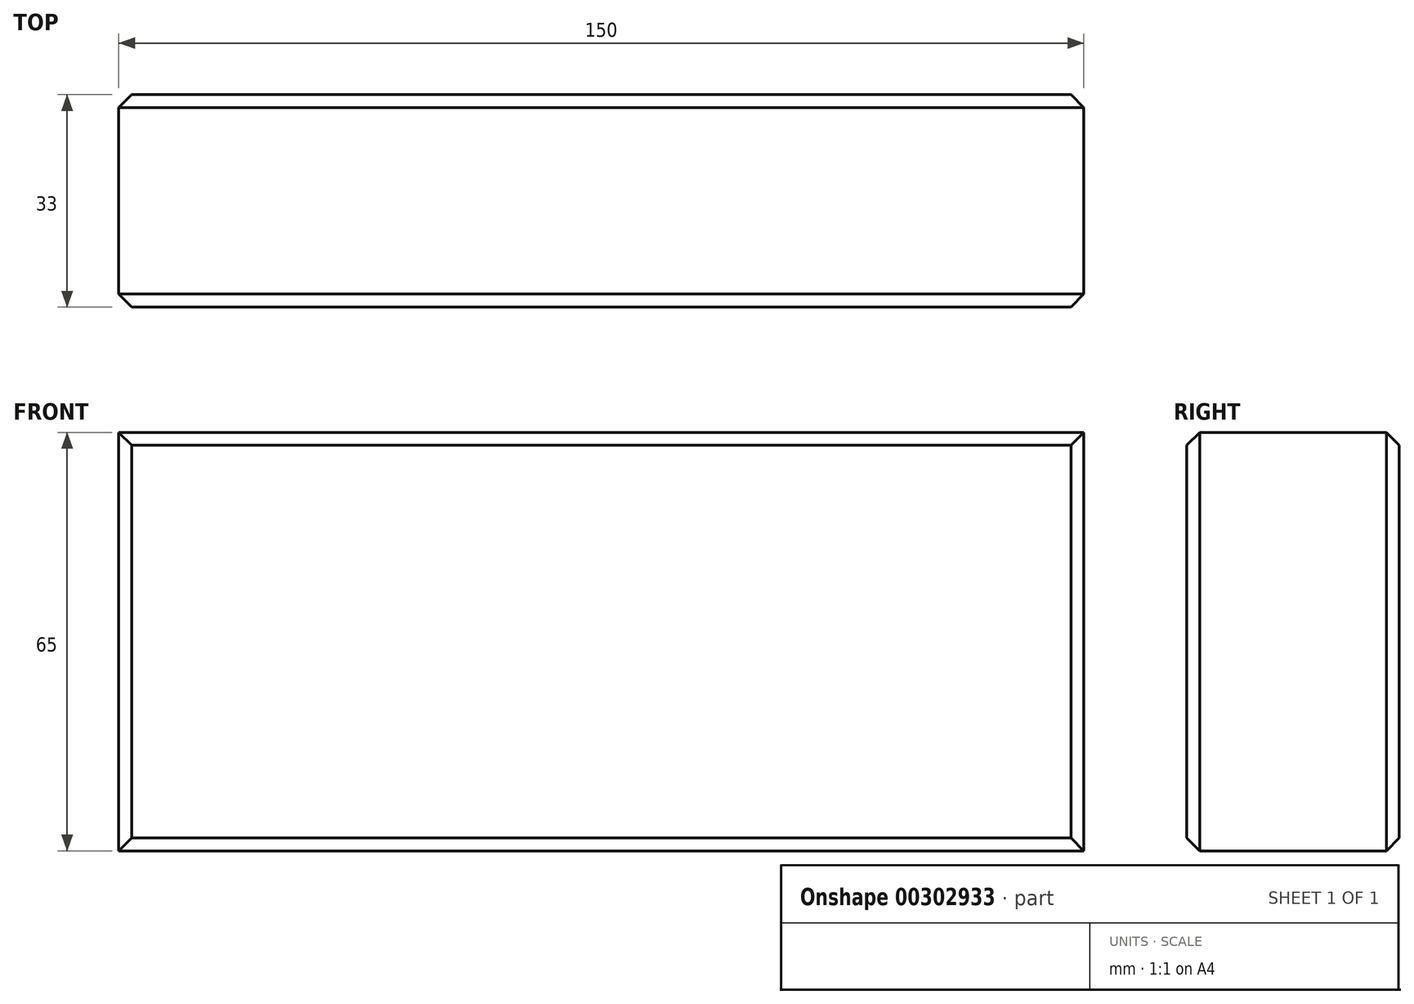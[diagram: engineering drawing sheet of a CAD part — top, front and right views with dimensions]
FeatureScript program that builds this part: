
annotation { "Feature Type Name" : "Feature", "Feature Type Description" : "" }
export const myFeature = defineFeature(function(context is Context, id is Id, definition is map)
    precondition{}
    {
        {
            var Q0;
            Q0=qCreatedBy(makeId("Front.planeOp"),FACE);
            var sketch = newSketch(context, id + "F0", { "sketchPlane" : qUnion([Q0])});
            skLineSegment(sketch, "E0.bottom", {"start": v(75, -32.5) * mm, "end": v(-75, -32.5) * mm});
            skLineSegment(sketch, "E0.top", {"start": v(75, 32.5) * mm, "end": v(-75, 32.5) * mm});
            skLineSegment(sketch, "E0.left", {"start": v(75, -32.5) * mm, "end": v(75, 32.5) * mm});
            skLineSegment(sketch, "E0.right", {"start": v(-75, -32.5) * mm, "end": v(-75, 32.5) * mm});
            skPoint(sketch, "E0.middle", {"position": v(0, 0) * mm});
            skSolve(sketch);
        }
        {
            var Q0;
            Q0 = qSketchRegion(id + "F0", true);
            extrude(context, id + "F1", {"entities" : qUnion([Q0]), "endBound" : BoundingType.SYMMETRIC, "depth" : 33 * mm});
        }
        {
            var Q0;
            Q0=makeQuery(id+"F1.opExtrude","CAP_FACE",FACE,{"disambiguationData":[OSD([sQuery(id+"F0.wireOp",EDGE,"E0.bottom"),sQuery(id+"F0.wireOp",EDGE,"E0.top"),sQuery(id+"F0.wireOp",EDGE,"E0.left"),sQuery(id+"F0.wireOp",EDGE,"E0.right")])],"isStart":false});
            var Q1;
            Q1=makeQuery(id+"F1.opExtrude","CAP_FACE",FACE,{"disambiguationData":[OSD([sQuery(id+"F0.wireOp",EDGE,"E0.bottom"),sQuery(id+"F0.wireOp",EDGE,"E0.top"),sQuery(id+"F0.wireOp",EDGE,"E0.left"),sQuery(id+"F0.wireOp",EDGE,"E0.right")])],"isStart":true});
            chamfer(context, id + "F2", {"entities" : qUnion([Q0, Q1]), "width" : 2 * mm, "tangentPropagation" : true});
        }
    });
